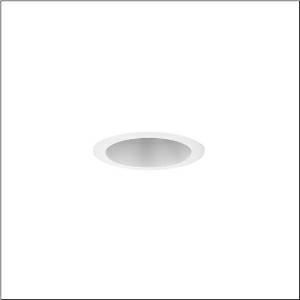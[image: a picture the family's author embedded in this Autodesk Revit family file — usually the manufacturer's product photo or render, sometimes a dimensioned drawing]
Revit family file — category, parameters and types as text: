
# Revit family: lunis_31-l_51dn16ee41b
name_source: partatom
category: Lighting Fixtures
units: mm (PartAtom-declared; Revit-internal decimal feet)

## family parameters
Cut with Voids When Loaded = No
Host = Face
Light Source = No
Part Type = Normal
Room Calculation Point = No
Round Connector Dimension = Use Diameter
Shared = No

## types (1)
- --- (1 x LED, 1600 lm, 12 W, 4000K)
    Apparent Load = 12 VA
    CIE Flux Codes = 76 93 99 100 100
    Color Rendering = 80
    Color Temperature = 4000K
    Default Elevation = 1800 mm
    Description = Lunis 31-L, downlight, light control with reflector, light emission: direct distribution, LED rated luminous flux: 1.600lm, light colour: 840, mains connection: 220..240V, AC/DC, 0/50..60Hz, housing, of aluminium, white, protection rating (complete): IP20, protection rating (on room side): IP54, insulation class (complete): insulation class II (safety insulation), certification: CE, ENEC, packaging unit: 1 piece
    Height = 0 mm  [stored 0 ft]
    Lamp = 1 x LED
    Lamp Light Flux = 1600 lm
    Lamp Power = 12 W
    Lamp count = 1
    Length = 188 mm  [stored 0.616798 ft]
    Luminous efficacy = 133 lm/W
    Manufacturer = Siteco
    ModVariant = No
    Model = 51DN16EE41B
    Mounting Place = Ceiling
    Mounting Type = Recessed
    Number of Poles = 1
    OnlyDefault = Yes
    Power Factor = 1
    Product Name = Lunis 31-L
    Product group = downlight
    ProductGroupID = 401
    Protection Class = Protection class II
    Protection Degree = IP 20
    RLX_Detail_Level = 1
    RLX_Emergency_Light_Flux = 0 lm
    RLX_Emergency_Type = 0
    RLX_Emergency_Type_DB = No
    RlxData = <blob elided: 22549 chars, md5=8244e092>
    Socket = socket
    Standby Power = 0 W
    System Light Flux = 1600 lm
    System Power = 12 W
    Type Comments = individual setting: luminous flux: 100 % | (OFF | ON) | 300 mA
    Type Image = l_1345911.jpg
    URL = http://relux.com
    VarID = @adj_029903
    Voltage = 0 V
    Weight = 0.00 kg
    Width = 0 mm  [stored 0 ft]

note: [stored X ft] marks values corroborated as IEEE doubles in the binary element streams (Revit-internal decimal feet)

## geometry (parser evidence)
native form markers: Blend x4, Sweep x10
no freeform markers — native parametric forms only
